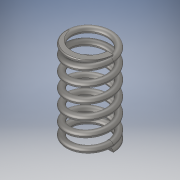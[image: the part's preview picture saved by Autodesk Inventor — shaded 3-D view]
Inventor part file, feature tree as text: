
AUTODESK INVENTOR PART (.ipt)
format: ipt  version: 2018 (Build 220112000, 112)  size: 701,440 bytes
history: native  units: in
note: dims shown in document units (in); Inventor stores cm internally (conversion verified against a paired STEP export)
features: extrude x1
ambient origin geometry x8: Origin, YZ Plane, XZ Plane, XY Plane, X Axis, Y Axis, Z Axis, Center Point
bodies: Solid1 (feature_tree)
feature tree (1):
  extrude  "Extrude1"  [1 undecoded]
note: 1 required parameter value undecoded (feature->parameter linkage not recoverable at this tier; creation-order binding heuristic only, values carry confidence <= 0.55)
